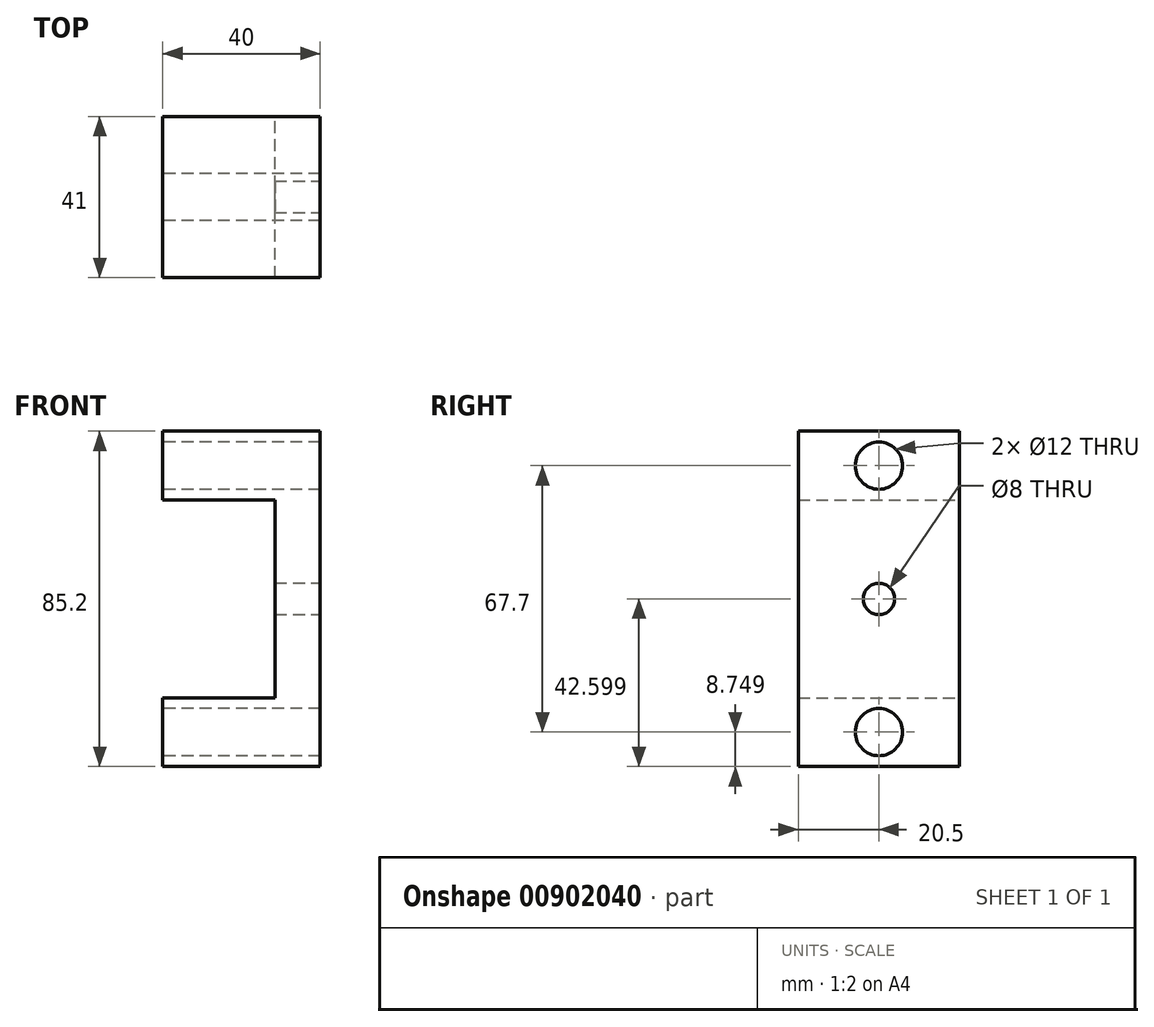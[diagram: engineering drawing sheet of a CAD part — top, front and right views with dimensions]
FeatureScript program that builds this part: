
annotation { "Feature Type Name" : "Feature", "Feature Type Description" : "" }
export const myFeature = defineFeature(function(context is Context, id is Id, definition is map)
    precondition{}
    {
        {
            var Q0;
            Q0=qCreatedBy(makeId("Front.planeOp"),FACE);
            var sketch = newSketch(context, id + "F0", { "sketchPlane" : qUnion([Q0])});
            skLineSegment(sketch, "E0", {"start": v(-62.09, 37.04) * mm, "end": v(-62.09, 19.54) * mm});
            skLineSegment(sketch, "E1", {"start": v(-62.09, 19.54) * mm, "end": v(-33.59, 19.54) * mm});
            skLineSegment(sketch, "E2", {"start": v(-33.59, 19.54) * mm, "end": v(-33.59, -30.66) * mm});
            skLineSegment(sketch, "E3", {"start": v(-33.59, -30.66) * mm, "end": v(-62.09, -30.66) * mm});
            skLineSegment(sketch, "E4", {"start": v(-62.09, -30.66) * mm, "end": v(-62.09, -48.16) * mm});
            skLineSegment(sketch, "E5", {"start": v(-62.09, -48.16) * mm, "end": v(-22.09, -48.16) * mm});
            skLineSegment(sketch, "E6", {"start": v(-22.09, -48.16) * mm, "end": v(-22.09, 37.04) * mm});
            skLineSegment(sketch, "E7", {"start": v(-22.09, 37.04) * mm, "end": v(-62.09, 37.04) * mm});
            skSolve(sketch);
        }
        {
            var Q0;
            Q0=makeQuery(id+"F0.imprint","IMPRINT",FACE,{"disambiguationData":[TD([[makeQuery(id+"F0.imprint","IMPRINT",EDGE,{"derivedFrom":sQuery(id+"F0.wireOp",EDGE,"E0")}),1.0]])]});
            extrude(context, id + "F1", {"entities" : qUnion([Q0]), "depth" : 41 * mm, "offsetDistance" : 25 * mm});
        }
        {
            var Q0;
            Q0=makeQuery(id+"F1.opExtrude","SWEPT_FACE",FACE,{"disambiguationData":[OSD([sQuery(id+"F0.wireOp",EDGE,"E0")])]});
            var sketch = newSketch(context, id + "F2", { "sketchPlane" : qUnion([Q0])});
            skPoint(sketch, "E8", {"position": v(20.5, 28.29) * mm});
            skSolve(sketch);
        }
        {
            var Q0;
            Q0=sQuery(id+"F2.wireOp",VERTEX,"E8");
            var Q1;
            Q1=makeQuery(id+"F1.opExtrude","SWEPT_BODY",BODY,{"disambiguationData":[OSD([sQuery(id+"F0.wireOp",EDGE,"E0"),sQuery(id+"F0.wireOp",EDGE,"E1"),sQuery(id+"F0.wireOp",EDGE,"E2"),sQuery(id+"F0.wireOp",EDGE,"E3"),sQuery(id+"F0.wireOp",EDGE,"E4"),sQuery(id+"F0.wireOp",EDGE,"E5"),sQuery(id+"F0.wireOp",EDGE,"E6"),sQuery(id+"F0.wireOp",EDGE,"E7")])]});
            hole(context, id + "F3", {"style" : HoleStyle.SIMPLE, "endStyle" : HoleEndStyle.THROUGH, "holeDiameter" : 12 * mm, "majorDiameter" : 5 * mm, "isTappedThrough" : true, "tappedDepth" : 12 * mm, "tapClearance" : 3, "startFromSketch" : true, "locations" : qUnion([Q0]), "scope" : qUnion([Q1])});
        }
        {
            var Q0;
            Q0=makeQuery(id+"F1.opExtrude","SWEPT_FACE",FACE,{"disambiguationData":[OSD([sQuery(id+"F0.wireOp",EDGE,"E4")])]});
            var sketch = newSketch(context, id + "F4", { "sketchPlane" : qUnion([Q0])});
            skPoint(sketch, "E9", {"position": v(20.5, -39.41) * mm});
            skSolve(sketch);
        }
        {
            var Q0;
            Q0=sQuery(id+"F4.wireOp",VERTEX,"E9");
            var Q1;
            Q1=makeQuery(id+"F1.opExtrude","SWEPT_BODY",BODY,{"disambiguationData":[OSD([sQuery(id+"F0.wireOp",EDGE,"E0"),sQuery(id+"F0.wireOp",EDGE,"E1"),sQuery(id+"F0.wireOp",EDGE,"E2"),sQuery(id+"F0.wireOp",EDGE,"E3"),sQuery(id+"F0.wireOp",EDGE,"E4"),sQuery(id+"F0.wireOp",EDGE,"E5"),sQuery(id+"F0.wireOp",EDGE,"E6"),sQuery(id+"F0.wireOp",EDGE,"E7")])]});
            hole(context, id + "F5", {"style" : HoleStyle.SIMPLE, "endStyle" : HoleEndStyle.THROUGH, "holeDiameter" : 12 * mm, "majorDiameter" : 5 * mm, "isTappedThrough" : true, "tappedDepth" : 12 * mm, "tapClearance" : 3, "startFromSketch" : true, "locations" : qUnion([Q0]), "scope" : qUnion([Q1])});
        }
        {
            var Q0;
            Q0=makeQuery(id+"F1.opExtrude","SWEPT_FACE",FACE,{"disambiguationData":[OSD([sQuery(id+"F0.wireOp",EDGE,"E6")])]});
            var sketch = newSketch(context, id + "F6", { "sketchPlane" : qUnion([Q0])});
            skPoint(sketch, "E10", {"position": v(-20.5, -5.56) * mm});
            skSolve(sketch);
        }
        {
            var Q0;
            Q0=sQuery(id+"F6.wireOp",VERTEX,"E10");
            var Q1;
            Q1=makeQuery(id+"F1.opExtrude","SWEPT_BODY",BODY,{"disambiguationData":[OSD([sQuery(id+"F0.wireOp",EDGE,"E0"),sQuery(id+"F0.wireOp",EDGE,"E1"),sQuery(id+"F0.wireOp",EDGE,"E2"),sQuery(id+"F0.wireOp",EDGE,"E3"),sQuery(id+"F0.wireOp",EDGE,"E4"),sQuery(id+"F0.wireOp",EDGE,"E5"),sQuery(id+"F0.wireOp",EDGE,"E6"),sQuery(id+"F0.wireOp",EDGE,"E7")])]});
            hole(context, id + "F7", {"style" : HoleStyle.SIMPLE, "endStyle" : HoleEndStyle.THROUGH, "holeDiameter" : 8 * mm, "majorDiameter" : 5 * mm, "isTappedThrough" : true, "tappedDepth" : 12 * mm, "tapClearance" : 3, "startFromSketch" : true, "locations" : qUnion([Q0]), "scope" : qUnion([Q1])});
        }
    });
